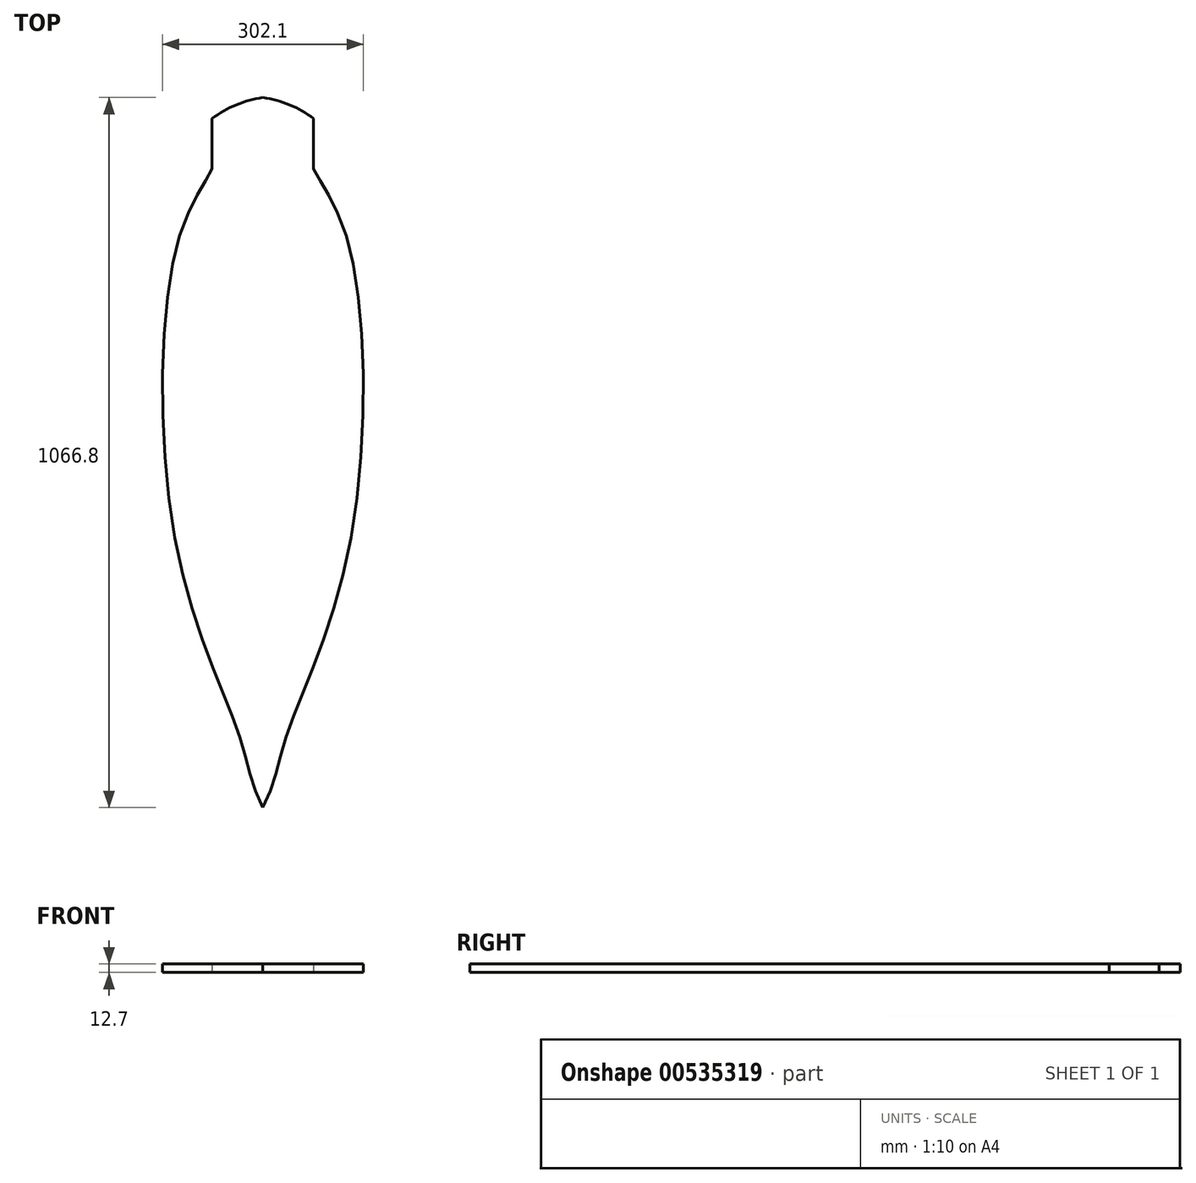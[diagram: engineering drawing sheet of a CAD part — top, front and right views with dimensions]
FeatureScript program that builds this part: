
annotation { "Feature Type Name" : "Feature", "Feature Type Description" : "" }
export const myFeature = defineFeature(function(context is Context, id is Id, definition is map)
    precondition{}
    {
        {
            var Q0;
            Q0=qCreatedBy(makeId("Top.planeOp"),FACE);
            var sketch = newSketch(context, id + "F0", { "sketchPlane" : qUnion([Q0])});
            skFitSpline(sketch, "E0", {"points": [v(-76.2, 165.75) * mm, v(-127, 58.43) * mm, v(-127, -416.13) * mm, v(-35.5, -686.1) * mm, v(0, -794.12) * mm], "startDerivative": vector(-188.13, -382.16) * mm, "endDerivative": vector(307.42, -570.45) * mm});
            skLineSegment(sketch, "E1", {"start": v(0, -794.12) * mm, "end": v(0, 272.68) * mm, "construction": true});
            skLineSegment(sketch, "E2", {"start": v(-76.2, 165.75) * mm, "end": v(-76.2, 240.95) * mm});
            skArc(sketch, "E3.trimOffspring", {"start": v(0, 272.68) * mm, "mid": v(-40.1, 261.6) * mm, "end": v(-76.2, 240.95) * mm});
            skLineSegment(sketch, "E4.MirrorCS", {"start": v(76.2, 165.75) * mm, "end": v(76.2, 240.95) * mm});
            skFitSpline(sketch, "E5.MirrorCS", {"points": [v(76.2, 165.75) * mm, v(127, 58.43) * mm, v(127, -416.13) * mm, v(35.5, -686.1) * mm, v(0, -794.12) * mm], "startDerivative": vector(188.13, -382.16) * mm, "endDerivative": vector(-307.42, -570.45) * mm});
            skArc(sketch, "E6.MirrorCS", {"start": v(0, 272.68) * mm, "mid": v(40.1, 261.6) * mm, "end": v(76.2, 240.95) * mm});
            skSolve(sketch);
        }
        {
            var Q0;
            Q0 = qSketchRegion(id + "F0", true);
            extrude(context, id + "F1", {"entities" : qUnion([Q0]), "depth" : 12.7 * mm, "offsetDistance" : 25.4 * mm});
        }
    });
